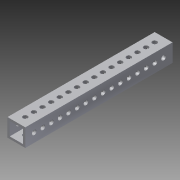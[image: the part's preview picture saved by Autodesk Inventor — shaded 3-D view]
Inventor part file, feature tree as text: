
AUTODESK INVENTOR PART (.ipt)
format: ipt  version: 2014 SP1 (Build 180222100, 222)  size: 187,392 bytes
history: native  units: in
note: dims shown in document units (in); Inventor stores cm internally (conversion verified against a paired STEP export)
features: extrude x3, sketch x2
ambient origin geometry x8: Origin, YZ Plane, XZ Plane, XY Plane, X Axis, Y Axis, Z Axis, Center Point
bodies: Solid1 (feature_tree)
feature tree (5):
  extrude  "Extrusion1"  Depth=1.0in
  extrude  "Extrusion2"  Depth=8.25in TaperAngle=0.0deg
  extrude  "Extrusion3"  Depth=1.0in
  sketch  "Sketch1"  dims[d0=1.0in d1=1.0in]
  sketch  "Sketch3"  dims[d2=0.125in d3=8.25in d4=0.0in d5=0.5in d7=0.26in d8=16.5in d9=0.0in d13=8.25in d14=6.2992in d16=0.4833in d17=0.3937in d19=1.0in d21=0.5in d22=8.25in d23=0.26in d24=6.2992in d26=0.4833in d27=0.3937in d29=1.0in d31=1.0in d32=0.0in]
